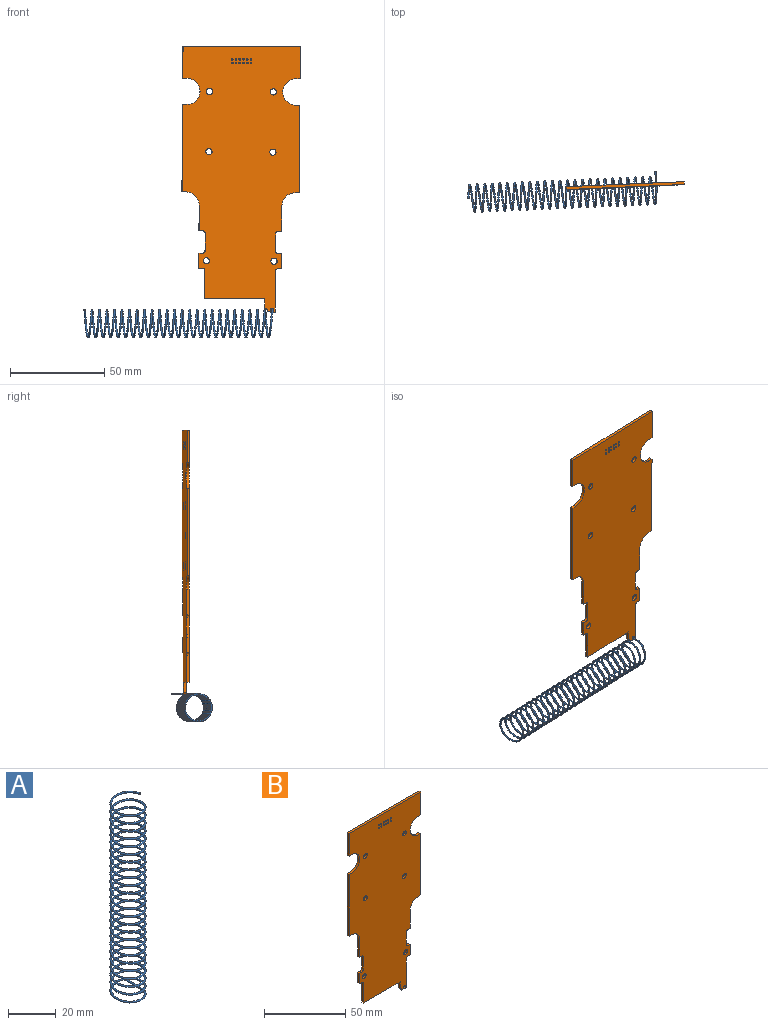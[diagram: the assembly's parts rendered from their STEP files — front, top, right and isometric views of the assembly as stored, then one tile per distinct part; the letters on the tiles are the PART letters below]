
ASSEMBLY  parts=2 mates=1
PART A: 4 faces, bbox 15.2x18.8x101.6 mm
  f0: plane 0.8x0.8mm, normal (0,-1,0), area 0.5mm2, adj f1
  f1: bspline ~101.6x17.56mm, area 2841.6mm2, adj f0,f2
  f2: cylinder r=0.4mm len=10mm, axis (0,-1,0), area 25.1mm2, adj f1,f3
  f3: plane 0.8x0.8mm, normal (0,1,0), area 0.5mm2, adj f2
PART B: 67 faces, bbox 62.4x1.5x141.1 mm
  f0: cylinder r=0.45mm len=1.5mm, axis (0,-1,0), area 4.2mm2, adj f20,f29
  f1: cylinder r=0.45mm len=1.5mm, axis (0,-1,0), area 4.2mm2, adj f20,f29
  f2: cylinder r=0.45mm len=1.5mm, axis (0,-1,0), area 4.2mm2, adj f20,f29
  f3: cylinder r=0.45mm len=1.5mm, axis (0,-1,0), area 4.2mm2, adj f20,f29
  f4: cylinder r=0.45mm len=1.5mm, axis (0,-1,0), area 4.2mm2, adj f20,f29
  f5: cylinder r=0.45mm len=1.5mm, axis (0,-1,0), area 4.2mm2, adj f20,f29
  f6: cylinder r=0.45mm len=1.5mm, axis (0,-1,0), area 4.2mm2, adj f20,f29
  f7: cylinder r=0.45mm len=1.5mm, axis (0,-1,0), area 4.2mm2, adj f20,f29
  f8: cylinder r=0.45mm len=1.5mm, axis (0,-1,0), area 4.2mm2, adj f20,f29
  f9: cylinder r=0.45mm len=1.5mm, axis (0,-1,0), area 4.2mm2, adj f20,f29
  f10: cylinder r=0.45mm len=1.5mm, axis (0,-1,0), area 4.2mm2, adj f20,f29
  f11: cylinder r=0.45mm len=1.5mm, axis (0,-1,0), area 4.2mm2, adj f20,f29
  f12: cylinder r=1.65mm len=3.3mm, axis (0,-1,0), area 15.6mm2, adj f20,f29
  f13: cylinder r=1.65mm len=3.3mm, axis (0,-1,0), area 15.6mm2, adj f20,f29
  f14: cylinder r=1.65mm len=3.3mm, axis (0,-1,0), area 15.6mm2, adj f20,f29
  f15: cylinder r=1.65mm len=3.3mm, axis (0,-1,0), area 15.6mm2, adj f20,f29
  f16: cylinder r=1.65mm len=3.3mm, axis (0,-1,0), area 15.6mm2, adj f20,f29
  f17: cylinder r=1.65mm len=3.3mm, axis (0,-1,0), area 15.6mm2, adj f20,f29
  f18: plane 5x1.5mm, normal (-1,0,0), area 7.5mm2, adj f19,f20,f29,f54
  f19: plane 31.9x1.5mm, normal (0,0,-1), area 47.9mm2, adj f18,f20,f22,f29
  f20: plane 141.08x62.4mm, normal (0,1,0), area 6765.1mm2, adj f0,f1,f2,f3,f4,f5,f6,f7
  f21: plane 9x1.5mm, normal (1,0,0), area 13.5mm2, adj f20,f29,f51,f64
  f22: plane 14.5x1.5mm, normal (-1,0,0), area 21.8mm2, adj f19,f20,f29,f57
  f23: cylinder r=7mm len=7mm, axis (0,-1,0), area 16.5mm2, adj f20,f29,f38,f49
  f24: plane 46.5x1.5mm, normal (1,0,0), area 69.8mm2, adj f20,f29,f34,f38
  f25: plane 46.5x1.5mm, normal (-1,0,0), area 69.8mm2, adj f20,f29,f30,f37
  f26: plane 17.08x1.5mm, normal (1,0,0), area 25.6mm2, adj f20,f29,f35,f65
  f27: plane 17.08x1.5mm, normal (-1,0,0), area 25.6mm2, adj f20,f29,f32,f65
  f28: plane 4x1.5mm, normal (0,0,-1), area 6mm2, adj f20,f29,f52,f53
  f29: plane 141.08x62.4mm, normal (0,-1,0), area 6924.5mm2, adj f0,f1,f2,f3,f4,f5,f6,f7
  f30: plane 2.2x1.5mm, normal (0,0,1), area 3.3mm2, adj f20,f25,f29,f31
  f31: cylinder r=7mm len=14mm, axis (0,-1,0), area 33mm2, adj f20,f29,f30,f32
  f32: plane 2.2x1.5mm, normal (0,0,-1), area 3.3mm2, adj f20,f27,f29,f31
  f33: cylinder r=7mm len=14mm, axis (0,-1,0), area 33mm2, adj f20,f29,f34,f35
  f34: plane 2.2x1.5mm, normal (0,0,1), area 3.3mm2, adj f20,f24,f29,f33
  f35: plane 2.2x1.5mm, normal (0,0,-1), area 3.3mm2, adj f20,f26,f29,f33
  f36: cylinder r=7mm len=7mm, axis (0,-1,0), area 16.5mm2, adj f20,f29,f37,f48
  f37: plane 2.2x1.5mm, normal (0,0,-1), area 3.3mm2, adj f20,f25,f29,f36
  f38: plane 2.2x1.5mm, normal (0,0,-1), area 3.3mm2, adj f20,f23,f24,f29
  f39: plane 6.4x4.15mm, normal (0,1,0), area 26.6mm2, adj f20
  f40: plane 6.4x4.15mm, normal (0,1,0), area 26.6mm2, adj f20
  f41: plane 6.4x4.15mm, normal (0,1,0), area 26.6mm2, adj f20
  f42: plane 6.4x4.15mm, normal (0,1,0), area 26.6mm2, adj f20
  f43: plane 6.4x4.15mm, normal (0,1,0), area 26.6mm2, adj f20
  f44: plane 6.4x4.15mm, normal (0,1,0), area 26.6mm2, adj f20
  f45: plane 9x1.5mm, normal (-1,0,0), area 13.5mm2, adj f20,f29,f46,f58
  f46: cylinder r=1.5mm len=1.5mm, axis (0,-1,0), area 3.5mm2, adj f20,f29,f45,f47
  f47: plane 1.8x1.5mm, normal (0,0,-1), area 2.7mm2, adj f20,f29,f46,f48
  f48: plane 13.5x1.5mm, normal (-1,0,0), area 20.3mm2, adj f20,f29,f36,f47
  f49: plane 13.5x1.5mm, normal (1,0,0), area 20.3mm2, adj f20,f23,f29,f50
  f50: plane 1.8x1.5mm, normal (0,0,-1), area 2.7mm2, adj f20,f29,f49,f51
  f51: cylinder r=1.5mm len=1.5mm, axis (0,-1,0), area 3.5mm2, adj f20,f21,f29,f50
  f52: plane 21.5x1.5mm, normal (1,0,0), area 32.3mm2, adj f20,f28,f29,f60
  f53: plane 1.5x0.5mm, normal (-1,0,0), area 0.8mm2, adj f20,f28,f29,f54
  f54: cylinder r=1.5mm len=1.5mm, axis (0,-1,0), area 3.5mm2, adj f18,f20,f29,f53
  f55: plane 8x1.5mm, normal (-1,0,0), area 12mm2, adj f20,f29,f56,f59
  f56: plane 1.8x1.5mm, normal (0,0,-1), area 2.7mm2, adj f20,f29,f55,f57
  f57: cylinder r=1.5mm len=1.5mm, axis (0,-1,0), area 3.5mm2, adj f20,f22,f29,f56
  f58: cylinder r=1.5mm len=1.5mm, axis (0,-1,0), area 3.5mm2, adj f20,f29,f45,f59
  f59: plane 1.8x1.5mm, normal (0,0,1), area 2.7mm2, adj f20,f29,f55,f58
  f60: cylinder r=1.5mm len=1.5mm, axis (0,-1,0), area 3.5mm2, adj f20,f29,f52,f61
  f61: plane 1.8x1.5mm, normal (0,0,-1), area 2.7mm2, adj f20,f29,f60,f62
  f62: plane 8x1.5mm, normal (1,0,0), area 12mm2, adj f20,f29,f61,f63
  f63: plane 1.8x1.5mm, normal (0,0,1), area 2.7mm2, adj f20,f29,f62,f64
  f64: cylinder r=1.5mm len=1.5mm, axis (0,-1,0), area 3.5mm2, adj f20,f21,f29,f63
  f65: plane 62.4x1.5mm, normal (0,0,1), area 93.6mm2, adj f20,f26,f27,f29
  f66: cylinder r=0.95mm len=1.9mm, axis (0,-1,0), area 9mm2, adj f20,f29
PLACE A rot(axis=(0.02,-1,0.02),90deg) t=(14.6,26.33,22.23)mm
PLACE B rot(axis=(0,0.16,0.99),2.5deg) t=(-3.12,30.25,-6.4)mm
MATE revolute A.f2 <-> B.f66  axis (0.04,-1,0) through (14.38,31.32,29.43)mm
